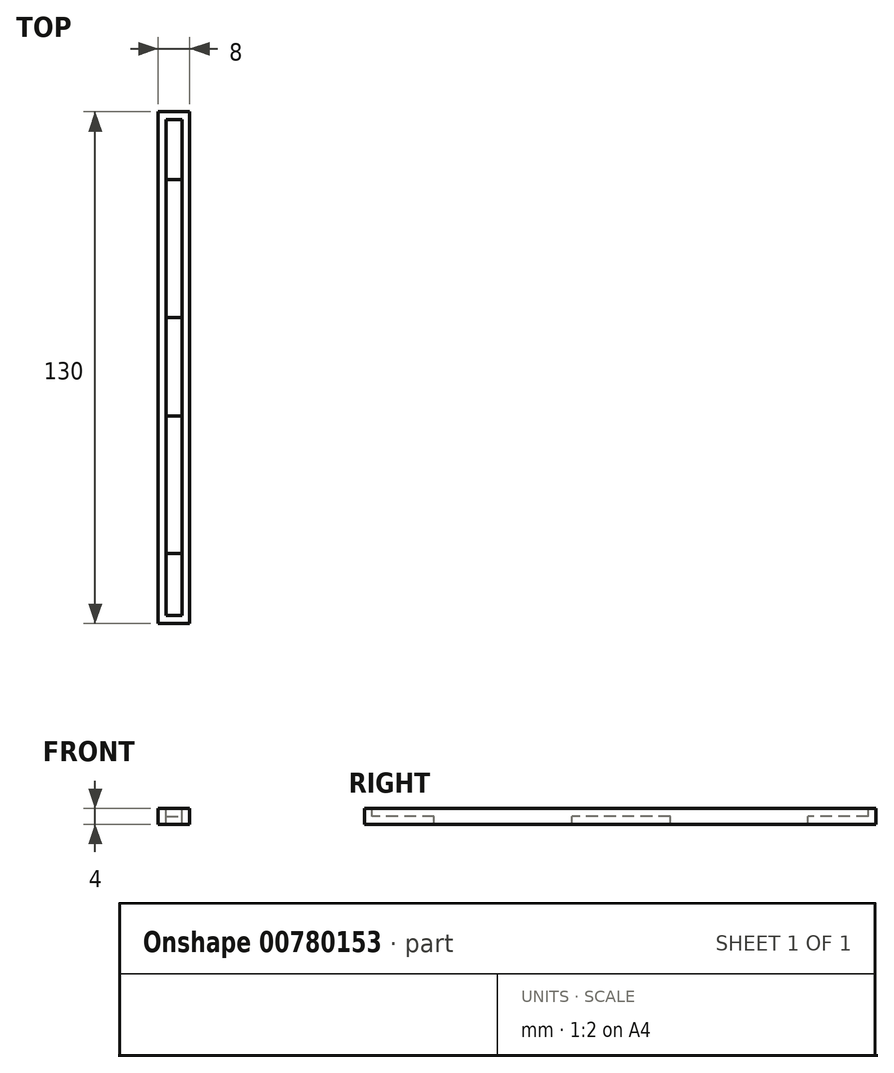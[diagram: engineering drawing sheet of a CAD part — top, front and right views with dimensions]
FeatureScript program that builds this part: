
annotation { "Feature Type Name" : "Feature", "Feature Type Description" : "" }
export const myFeature = defineFeature(function(context is Context, id is Id, definition is map)
    precondition{}
    {
        {
            var Q0;
            Q0=qCreatedBy(makeId("Top.planeOp"),FACE);
            var sketch = newSketch(context, id + "F0", { "sketchPlane" : qUnion([Q0])});
            skLineSegment(sketch, "E0.bottom", {"start": v(-4, 65) * mm, "end": v(4, 65) * mm});
            skLineSegment(sketch, "E0.top", {"start": v(-4, -65) * mm, "end": v(4, -65) * mm});
            skLineSegment(sketch, "E0.left", {"start": v(-4, 65) * mm, "end": v(-4, -65) * mm});
            skLineSegment(sketch, "E0.right", {"start": v(4, 65) * mm, "end": v(4, -65) * mm});
            skSolve(sketch);
        }
        {
            var Q0;
            Q0=makeQuery(id+"F0.imprint","IMPRINT",FACE,{"disambiguationData":[TD([[makeQuery(id+"F0.imprint","IMPRINT",EDGE,{"derivedFrom":sQuery(id+"F0.wireOp",EDGE,"E0.bottom")}),-1.0]])]});
            extrude(context, id + "F1", {"entities" : qUnion([Q0]), "depth" : 4 * mm, "offsetDistance" : 25 * mm});
        }
        {
            var Q0;
            Q0=makeQuery(id+"F1.opExtrude","CAP_FACE",FACE,{"disambiguationData":[OSD([sQuery(id+"F0.wireOp",EDGE,"E0.bottom"),sQuery(id+"F0.wireOp",EDGE,"E0.top"),sQuery(id+"F0.wireOp",EDGE,"E0.left"),sQuery(id+"F0.wireOp",EDGE,"E0.right")])],"isStart":false});
            var sketch = newSketch(context, id + "F2", { "sketchPlane" : qUnion([Q0])});
            skLineSegment(sketch, "E1.bottom", {"start": v(-2, 63) * mm, "end": v(2, 63) * mm});
            skLineSegment(sketch, "E1.top", {"start": v(-2, -63) * mm, "end": v(2, -63) * mm});
            skLineSegment(sketch, "E1.left", {"start": v(-2, 63) * mm, "end": v(-2, -63) * mm});
            skLineSegment(sketch, "E1.right", {"start": v(2, 63) * mm, "end": v(2, -63) * mm});
            skSolve(sketch);
        }
        {
            var Q0;
            Q0=makeQuery(id+"F2.imprint","IMPRINT",FACE,{"disambiguationData":[TD([[makeQuery(id+"F2.imprint","IMPRINT",EDGE,{"derivedFrom":sQuery(id+"F2.wireOp",EDGE,"E1.bottom")}),-1.0]])]});
            extrude(context, id + "F3", {"entities" : qUnion([Q0]), "operationType" : NewBodyOperationType.REMOVE, "oppositeDirection" : true, "depth" : 2 * mm, "offsetDistance" : 25 * mm});
        }
        {
            var Q0;
            Q0=makeQuery(id+"F3.boolean.opBoolean","COPY",FACE,{"derivedFrom":makeQuery(id+"F3.opExtrude","CAP_FACE",FACE,{"disambiguationData":[OSD([sQuery(id+"F2.wireOp",EDGE,"E1.bottom"),sQuery(id+"F2.wireOp",EDGE,"E1.top"),sQuery(id+"F2.wireOp",EDGE,"E1.left"),sQuery(id+"F2.wireOp",EDGE,"E1.right")])],"isStart":false})});
            var sketch = newSketch(context, id + "F4", { "sketchPlane" : qUnion([Q0])});
            skLineSegment(sketch, "E2.bottom", {"start": v(-2, 47.73) * mm, "end": v(2, 47.73) * mm});
            skLineSegment(sketch, "E2.top", {"start": v(-2, 12.73) * mm, "end": v(2, 12.73) * mm});
            skLineSegment(sketch, "E2.left", {"start": v(-2, 47.73) * mm, "end": v(-2, 12.73) * mm});
            skLineSegment(sketch, "E2.right", {"start": v(2, 47.73) * mm, "end": v(2, 12.73) * mm});
            skLineSegment(sketch, "E3.1.0.0", {"start": v(-2, -12.27) * mm, "end": v(2, -12.27) * mm});
            skLineSegment(sketch, "E3.1.0.1", {"start": v(-2, -47.27) * mm, "end": v(2, -47.27) * mm});
            skLineSegment(sketch, "E3.1.0.2", {"start": v(-2, -12.27) * mm, "end": v(-2, -47.27) * mm});
            skLineSegment(sketch, "E3.1.0.3", {"start": v(2, -12.27) * mm, "end": v(2, -47.27) * mm});
            skLineSegment(sketch, "E3.direction1", {"start": v(-2, 12.73) * mm, "end": v(-2, -47.27) * mm, "construction": true});
            skSolve(sketch);
        }
        {
            var Q0;
            Q0=makeQuery(id+"F4.imprint","IMPRINT",FACE,{"disambiguationData":[TD([[makeQuery(id+"F4.imprint","IMPRINT",EDGE,{"derivedFrom":sQuery(id+"F4.wireOp",EDGE,"E3.1.0.0")}),-1.0]])]});
            var Q1;
            Q1=makeQuery(id+"F4.imprint","IMPRINT",FACE,{"disambiguationData":[TD([[makeQuery(id+"F4.imprint","IMPRINT",EDGE,{"derivedFrom":sQuery(id+"F4.wireOp",EDGE,"E2.bottom")}),-1.0]])]});
            extrude(context, id + "F5", {"entities" : qUnion([Q0, Q1]), "operationType" : NewBodyOperationType.REMOVE, "endBound" : BoundingType.THROUGH_ALL, "oppositeDirection" : true, "depth" : 25 * mm, "offsetDistance" : 25 * mm});
        }
    });
